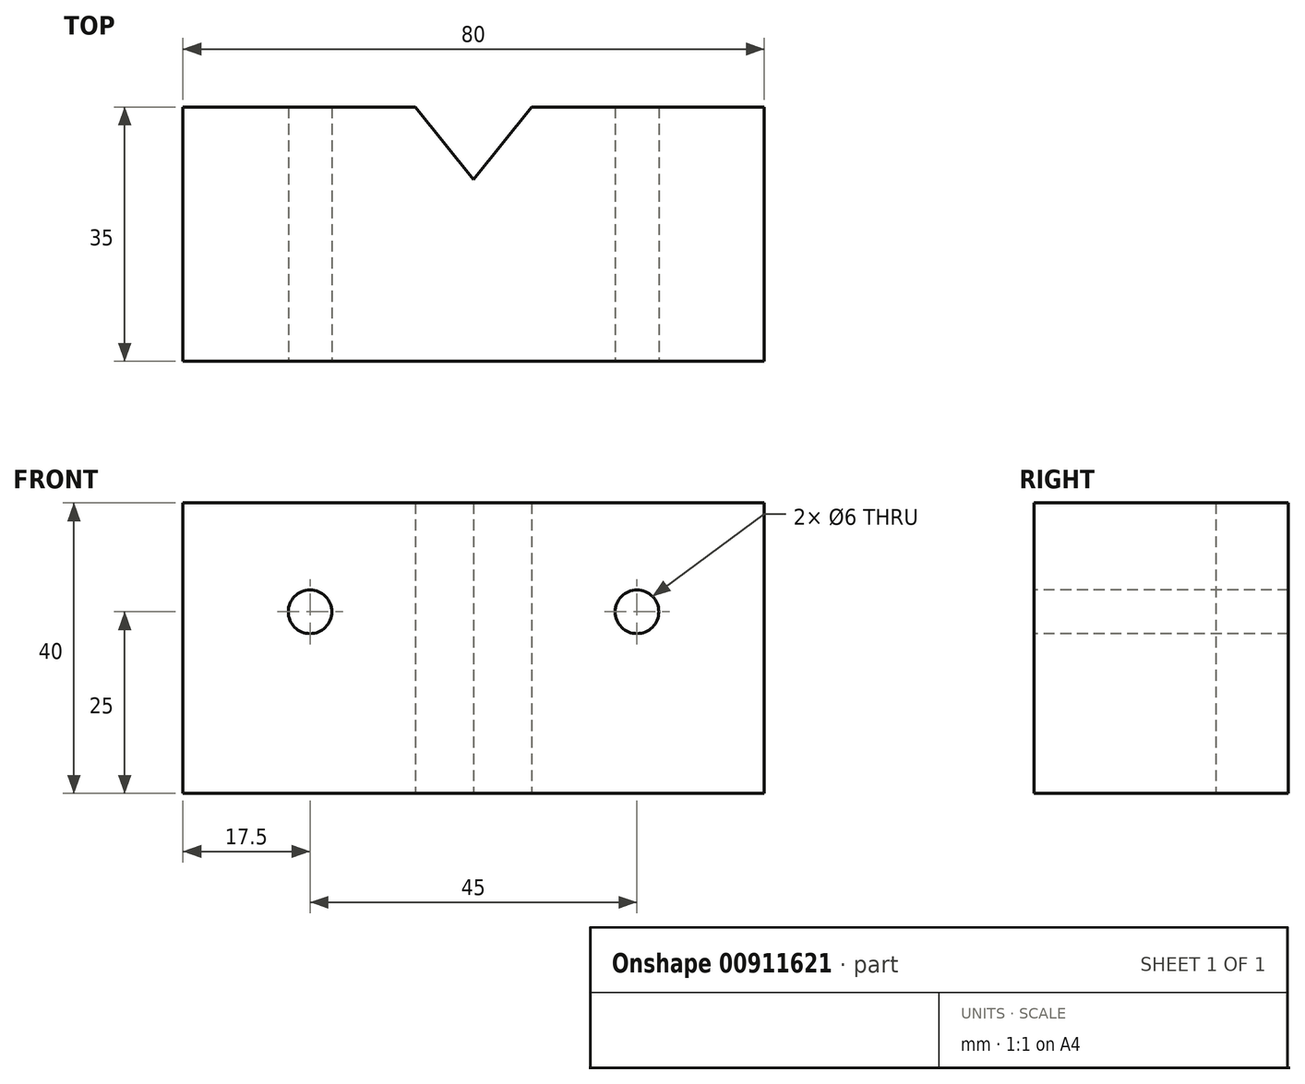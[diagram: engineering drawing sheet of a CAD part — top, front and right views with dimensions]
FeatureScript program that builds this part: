
annotation { "Feature Type Name" : "Feature", "Feature Type Description" : "" }
export const myFeature = defineFeature(function(context is Context, id is Id, definition is map)
    precondition{}
    {
        {
            var Q0;
            Q0=qCreatedBy(makeId("Top.planeOp"),FACE);
            var sketch = newSketch(context, id + "F0", { "sketchPlane" : qUnion([Q0])});
            skLineSegment(sketch, "E0.bottom", {"start": v(0, 0) * mm, "end": v(80, 0) * mm});
            skLineSegment(sketch, "E0.top", {"start": v(0, 35) * mm, "end": v(32, 35) * mm});
            skLineSegment(sketch, "E0.left", {"start": v(0, 0) * mm, "end": v(0, 35) * mm});
            skLineSegment(sketch, "E0.right", {"start": v(80, 0) * mm, "end": v(80, 35) * mm});
            skPoint(sketch, "E1", {"position": v(40, 35) * mm});
            skPoint(sketch, "E2", {"position": v(80, 17.5) * mm});
            skLineSegment(sketch, "E3", {"start": v(40, 25) * mm, "end": v(32, 35) * mm});
            skLineSegment(sketch, "E4", {"start": v(40, 25) * mm, "end": v(48, 35) * mm});
            skLineSegment(sketch, "E5", {"start": v(40, 35) * mm, "end": v(40, 0) * mm, "construction": true});
            skLineSegment(sketch, "E6.trimOffspring", {"start": v(48, 35) * mm, "end": v(80, 35) * mm});
            skSolve(sketch);
        }
        {
            var Q0;
            Q0 = qSketchRegion(id + "F0", true);
            extrude(context, id + "F1", {"entities" : qUnion([Q0]), "depth" : 40 * mm, "offsetDistance" : 25 * mm});
        }
        {
            var Q0;
            Q0=makeQuery(id+"F1.opExtrude","SWEPT_FACE",FACE,{"disambiguationData":[OSD([sQuery(id+"F0.wireOp",EDGE,"E0.bottom")])]});
            var sketch = newSketch(context, id + "F2", { "sketchPlane" : qUnion([Q0])});
            skCircle(sketch, "E7", {"center": v(17.5, 25) * mm, "radius": 3 * mm});
            skCircle(sketch, "E8", {"center": v(62.5, 25) * mm, "radius": 3 * mm});
            skLineSegment(sketch, "E9", {"start": v(40, 40) * mm, "end": v(40, 0) * mm, "construction": true});
            skSolve(sketch);
        }
        {
            var Q0;
            Q0 = qSketchRegion(id + "F2", true);
            extrude(context, id + "F3", {"entities" : qUnion([Q0]), "operationType" : NewBodyOperationType.REMOVE, "endBound" : BoundingType.THROUGH_ALL, "oppositeDirection" : true, "depth" : 25 * mm, "offsetDistance" : 25 * mm});
        }
    });
